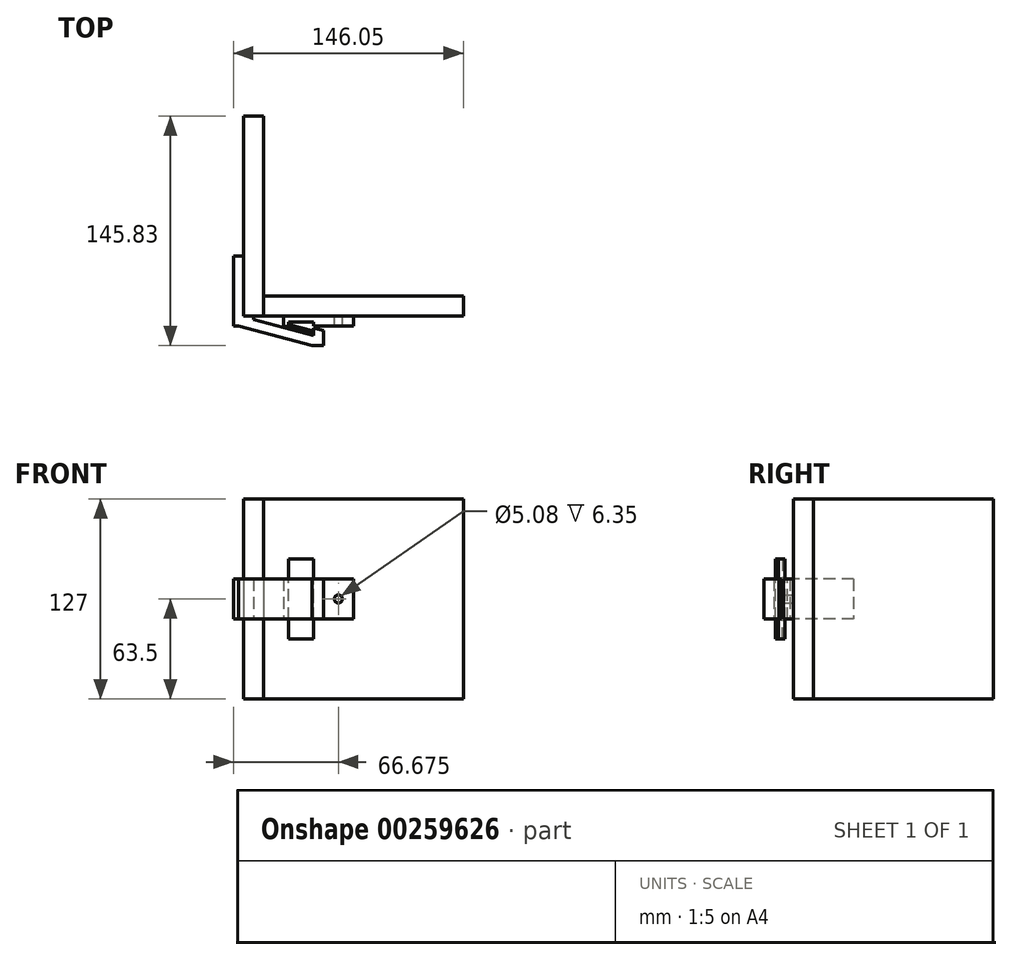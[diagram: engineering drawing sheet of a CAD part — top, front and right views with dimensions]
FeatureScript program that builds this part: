
annotation { "Feature Type Name" : "Feature", "Feature Type Description" : "" }
export const myFeature = defineFeature(function(context is Context, id is Id, definition is map)
    precondition{}
    {
        {
            var Q0;
            Q0=qCreatedBy(makeId("Top.planeOp"),FACE);
            var sketch = newSketch(context, id + "F0", { "sketchPlane" : qUnion([Q0])});
            skLineSegment(sketch, "E0", {"start": v(0, 127) * mm, "end": v(0, 0) * mm});
            skLineSegment(sketch, "E1", {"start": v(0, 0) * mm, "end": v(12.7, 0) * mm});
            skLineSegment(sketch, "E2", {"start": v(12.7, 0) * mm, "end": v(12.7, 127) * mm});
            skLineSegment(sketch, "E3", {"start": v(12.7, 127) * mm, "end": v(0, 127) * mm});
            skLineSegment(sketch, "E4.bottom", {"start": v(12.7, 0) * mm, "end": v(139.7, 0) * mm});
            skLineSegment(sketch, "E4.top", {"start": v(12.7, 12.7) * mm, "end": v(139.7, 12.7) * mm});
            skLineSegment(sketch, "E4.left", {"start": v(12.7, 0) * mm, "end": v(12.7, 12.7) * mm});
            skLineSegment(sketch, "E4.right", {"start": v(139.7, 0) * mm, "end": v(139.7, 12.7) * mm});
            skSolve(sketch);
        }
        {
            var Q0;
            Q0=makeQuery(id+"F0.imprint","IMPRINT",FACE,{"disambiguationData":[TD([[makeQuery(id+"F0.imprint","IMPRINT",EDGE,{"derivedFrom":sQuery(id+"F0.wireOp",EDGE,"E0")}),1.0]])]});
            extrude(context, id + "F1", {"entities" : qUnion([Q0]), "depth" : 127 * mm});
        }
        {
            var Q0;
            Q0=makeQuery(id+"F0.imprint","IMPRINT",FACE,{"disambiguationData":[TD([[makeQuery(id+"F0.imprint","IMPRINT",EDGE,{"derivedFrom":sQuery(id+"F0.wireOp",EDGE,"E4.bottom")}),1.0]])]});
            extrude(context, id + "F2", {"entities" : qUnion([Q0]), "depth" : 127 * mm});
        }
        {
            var Q0;
            Q0=makeQuery(id+"F2.opExtrude","SWEPT_FACE",FACE,{"disambiguationData":[OSD([sQuery(id+"F0.wireOp",EDGE,"E4.bottom")])]});
            var sketch = newSketch(context, id + "F3", { "sketchPlane" : qUnion([Q0])});
            skLineSegment(sketch, "E5", {"start": v(12.7, 63.5) * mm, "end": v(152.97, 63.5) * mm, "construction": true});
            skLineSegment(sketch, "E6.bottom", {"start": v(25.4, 76.2) * mm, "end": v(69.85, 76.2) * mm});
            skLineSegment(sketch, "E6.top", {"start": v(25.4, 50.8) * mm, "end": v(69.85, 50.8) * mm});
            skLineSegment(sketch, "E6.left", {"start": v(25.4, 76.2) * mm, "end": v(25.4, 50.8) * mm});
            skLineSegment(sketch, "E6.right", {"start": v(69.85, 76.2) * mm, "end": v(69.85, 50.8) * mm});
            skCircle(sketch, "E7", {"center": v(60.33, 63.5) * mm, "radius": 2.54 * mm});
            skSolve(sketch);
        }
        {
            var Q0;
            Q0 = qSketchRegion(id + "F3", true);
            extrude(context, id + "F4", {"entities" : qUnion([Q0]), "depth" : 6.35 * mm});
        }
        {
            var Q0;
            Q0=makeQuery(id+"F4.opExtrude","SWEPT_FACE",FACE,{"disambiguationData":[OSD([sQuery(id+"F3.wireOp",EDGE,"E6.bottom")])]});
            var sketch = newSketch(context, id + "F5", { "sketchPlane" : qUnion([Q0])});
            skLineSegment(sketch, "E8", {"start": v(25.4, -6.35) * mm, "end": v(44.45, -11.43) * mm});
            skLineSegment(sketch, "E9", {"start": v(44.45, -11.43) * mm, "end": v(44.45, -6.35) * mm});
            skLineSegment(sketch, "E10", {"start": v(44.45, -6.35) * mm, "end": v(25.4, -6.35) * mm});
            skSolve(sketch);
        }
        {
            var Q0;
            Q0=makeQuery(id+"F5.imprint","IMPRINT",FACE,{"disambiguationData":[TD([[makeQuery(id+"F5.imprint","IMPRINT",EDGE,{"derivedFrom":sQuery(id+"F5.wireOp",EDGE,"E8")}),1.0]])]});
            var Q1;
            Q1=makeQuery(id+"F4.opExtrude","SWEPT_FACE",FACE,{"disambiguationData":[OSD([sQuery(id+"F3.wireOp",EDGE,"E6.top")])]});
            extrude(context, id + "F6", {"entities" : qUnion([Q0]), "operationType" : NewBodyOperationType.ADD, "endBound" : BoundingType.UP_TO_SURFACE, "oppositeDirection" : true, "endBoundEntityFace" : qUnion([Q1]), "depth" : 25.4 * mm});
        }
        {
            var Q0;
            Q0=makeQuery(id+"F6.boolean.opBoolean","MERGE",FACE,{"derivedFrom":[makeQuery(id+"F4.opExtrude","SWEPT_FACE",FACE,{"disambiguationData":[OSD([sQuery(id+"F3.wireOp",EDGE,"E6.bottom")])]}),makeQuery(id+"F6.opExtrude","CAP_FACE",FACE,{"disambiguationData":[OSD([sQuery(id+"F5.wireOp",EDGE,"E8"),sQuery(id+"F5.wireOp",EDGE,"E9"),sQuery(id+"F5.wireOp",EDGE,"E10")])],"isStart":true})]});
            var sketch = newSketch(context, id + "F7", { "sketchPlane" : qUnion([Q0])});
            skLineSegment(sketch, "E11", {"start": v(44.45, -9.59) * mm, "end": v(28.58, -5.36) * mm});
            skLineSegment(sketch, "E12", {"start": v(28.58, -5.36) * mm, "end": v(28.58, -3.81) * mm});
            skLineSegment(sketch, "E13", {"start": v(28.58, -3.81) * mm, "end": v(44.45, -3.81) * mm});
            skLineSegment(sketch, "E14", {"start": v(44.45, -3.81) * mm, "end": v(44.45, -9.59) * mm});
            skSolve(sketch);
        }
        {
            var Q0;
            Q0 = qSketchRegion(id + "F7", true);
            extrude(context, id + "F8", {"entities" : qUnion([Q0]), "operationType" : NewBodyOperationType.REMOVE, "endBound" : BoundingType.THROUGH_ALL, "oppositeDirection" : true, "depth" : 25.4 * mm});
        }
        {
            var Q0;
            Q0=makeQuery(id+"F6.boolean.opBoolean","MERGE",FACE,{"derivedFrom":[makeQuery(id+"F4.opExtrude","SWEPT_FACE",FACE,{"disambiguationData":[OSD([sQuery(id+"F3.wireOp",EDGE,"E6.bottom")])]}),makeQuery(id+"F6.opExtrude","CAP_FACE",FACE,{"disambiguationData":[OSD([sQuery(id+"F5.wireOp",EDGE,"E8"),sQuery(id+"F5.wireOp",EDGE,"E9"),sQuery(id+"F5.wireOp",EDGE,"E10")])],"isStart":true})]});
            var sketch = newSketch(context, id + "F9", { "sketchPlane" : qUnion([Q0])});
            skLineSegment(sketch, "E15.0", {"start": v(44.45, -9.59) * mm, "end": v(28.58, -5.36) * mm});
            skLineSegment(sketch, "E16", {"start": v(28.58, -5.36) * mm, "end": v(28.58, -7.2) * mm});
            skLineSegment(sketch, "E17", {"start": v(28.58, -7.2) * mm, "end": v(44.45, -11.43) * mm});
            skLineSegment(sketch, "E18", {"start": v(44.45, -11.43) * mm, "end": v(44.45, -9.59) * mm});
            skPoint(sketch, "E15.1.end.orphan", {"position": v(28.58, -3.81) * mm});
            skPoint(sketch, "E15.1.start.orphan", {"position": v(28.58, -5.36) * mm});
            skPoint(sketch, "E15.2.end.orphan", {"position": v(44.45, -3.81) * mm});
            skPoint(sketch, "E15.2.start.orphan", {"position": v(28.58, -3.81) * mm});
            skPoint(sketch, "E15.3.end.orphan", {"position": v(44.45, -9.59) * mm});
            skPoint(sketch, "E15.3.start.orphan", {"position": v(44.45, -3.81) * mm});
            skSolve(sketch);
        }
        {
            var Q0;
            Q0 = qSketchRegion(id + "F9", true);
            extrude(context, id + "F10", {"entities" : qUnion([Q0]), "operationType" : NewBodyOperationType.ADD, "depth" : 12.7 * mm});
        }
        {
            var Q0;
            Q0=makeQuery(id+"F4.opExtrude","CAP_EDGE",EDGE,{"disambiguationData":[OSD([sQuery(id+"F3.wireOp",EDGE,"E6.right")])],"isStart":false});
            cPoint(context, id + "F11", {"entities" : qUnion([Q0]), "parameter" : 0.5});
        }
        {
            var Q0;
            Q0 = qCreatedBy(id + "F11" ,VERTEX);
            var Q1;
            Q1=qCreatedBy(makeId("Top.planeOp"),FACE);
            cPlane(context, id + "F12", {"entities" : qUnion([Q0, Q1]), "cplaneType" : CPlaneType.PLANE_POINT, "offset" : 25.4 * mm, "width" : 152.4 * mm, "height" : 152.4 * mm});
        }
        {
            var Q0;
            Q0=makeQuery(id+"F4.opExtrude","SWEPT_BODY",BODY,{"disambiguationData":[OSD([sQuery(id+"F3.wireOp",EDGE,"E6.bottom"),sQuery(id+"F3.wireOp",EDGE,"E6.top"),sQuery(id+"F3.wireOp",EDGE,"E6.left"),sQuery(id+"F3.wireOp",EDGE,"E6.right"),sQuery(id+"F3.wireOp",EDGE,"E7")])]});
            var Q1;
            Q1=qCreatedBy(id+"F12.planeOp",FACE);
            mirror(context, id + "F13", {"operationType" : NewBodyOperationType.ADD, "entities" : qUnion([Q0]), "mirrorPlane" : qUnion([Q1])});
        }
        {
            var Q0;
            Q0=qCreatedBy(id+"F12.planeOp",FACE);
            var sketch = newSketch(context, id + "F14", { "sketchPlane" : qUnion([Q0])});
            skLineSegment(sketch, "E19", {"start": v(0, 38.1) * mm, "end": v(-6.35, 38.1) * mm});
            skLineSegment(sketch, "E20", {"start": v(-6.35, 38.1) * mm, "end": v(-6.35, -6.35) * mm});
            skLineSegment(sketch, "E21", {"start": v(-6.35, -6.35) * mm, "end": v(-3.19, -6.35) * mm});
            skLineSegment(sketch, "E22", {"start": v(44.45, -12.48) * mm, "end": v(44.45, -7.56) * mm});
            skLineSegment(sketch, "E23", {"start": v(44.45, -7.56) * mm, "end": v(50.8, -9.25) * mm});
            skLineSegment(sketch, "E24", {"start": v(50.8, -9.25) * mm, "end": v(50.8, -18.83) * mm});
            skLineSegment(sketch, "E25", {"start": v(50.8, -18.83) * mm, "end": v(43.62, -18.83) * mm});
            skLineSegment(sketch, "E26", {"start": v(0, 38.1) * mm, "end": v(0, 0) * mm});
            skLineSegment(sketch, "E27", {"start": v(6.35, -2.32) * mm, "end": v(44.45, -12.48) * mm});
            skLineSegment(sketch, "E28", {"start": v(6.35, -2.32) * mm, "end": v(6.35, 0) * mm});
            skLineSegment(sketch, "E29", {"start": v(6.35, 0) * mm, "end": v(0, 0) * mm});
            skPoint(sketch, "E30.orphan", {"position": v(-2.36, 0) * mm});
            skLineSegment(sketch, "E31", {"start": v(-3.19, -6.35) * mm, "end": v(43.62, -18.83) * mm});
            skPoint(sketch, "E32.orphan", {"position": v(0, -18.83) * mm});
            skLineSegment(sketch, "E33", {"start": v(-3.19, -6.35) * mm, "end": v(-3.19, -6.35) * mm});
            skPoint(sketch, "E34", {"position": v(-3.19, -6.35) * mm});
            skSolve(sketch);
        }
        {
            var Q0;
            Q0 = qSketchRegion(id + "F14", true);
            extrude(context, id + "F15", {"entities" : qUnion([Q0]), "endBound" : BoundingType.SYMMETRIC, "depth" : 25.4 * mm});
        }
    });
